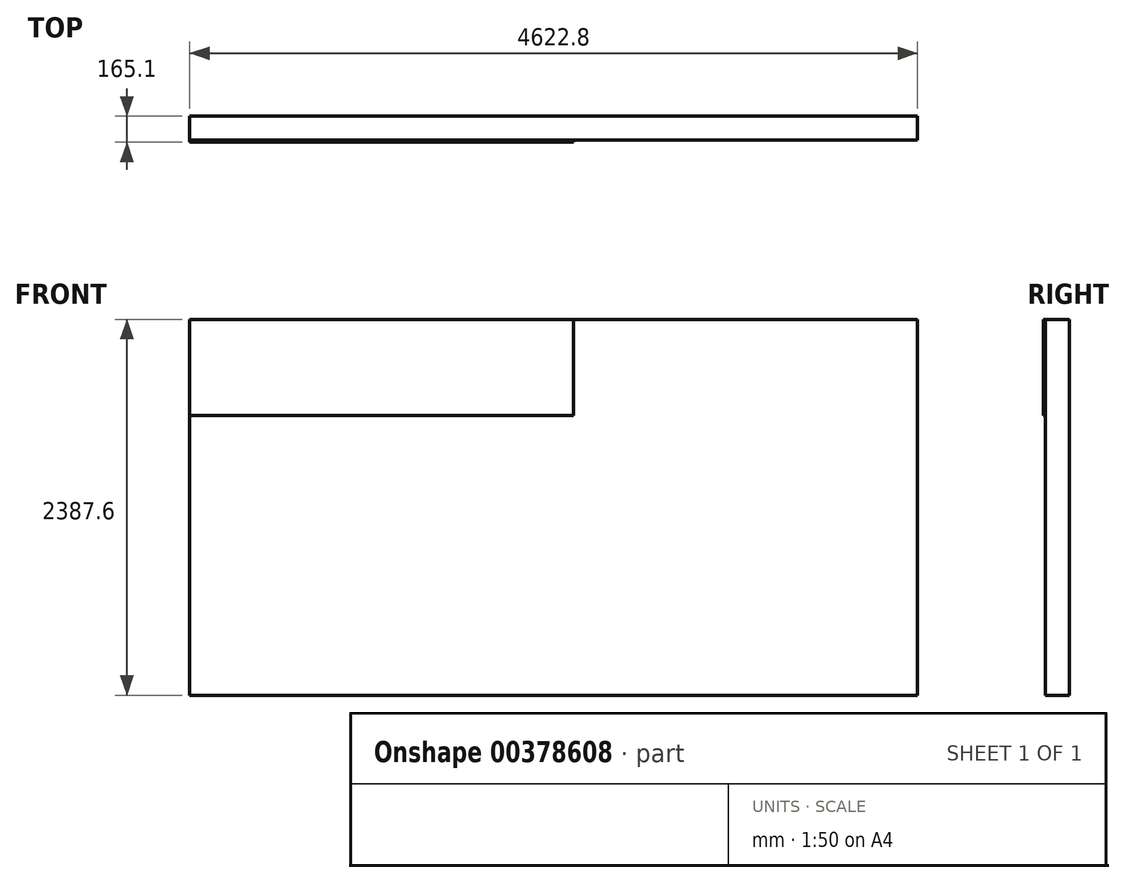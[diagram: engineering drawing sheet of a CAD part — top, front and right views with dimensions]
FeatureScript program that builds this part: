
annotation { "Feature Type Name" : "Feature", "Feature Type Description" : "" }
export const myFeature = defineFeature(function(context is Context, id is Id, definition is map)
    precondition{}
    {
        {
            var Q0;
            Q0=qCreatedBy(makeId("Front.planeOp"),FACE);
            var sketch = newSketch(context, id + "F0", { "sketchPlane" : qUnion([Q0])});
            skLineSegment(sketch, "E0.bottom", {"start": v(0, 0) * mm, "end": v(4622.8, 0) * mm});
            skLineSegment(sketch, "E0.top", {"start": v(0, 2387.6) * mm, "end": v(4622.8, 2387.6) * mm});
            skLineSegment(sketch, "E0.left", {"start": v(0, 0) * mm, "end": v(0, 2387.6) * mm});
            skLineSegment(sketch, "E0.right", {"start": v(4622.8, 0) * mm, "end": v(4622.8, 2387.6) * mm});
            skSolve(sketch);
        }
        {
            var Q0;
            Q0=makeQuery(id+"F0.imprint","IMPRINT",FACE,{"disambiguationData":[TD([[makeQuery(id+"F0.imprint","IMPRINT",EDGE,{"derivedFrom":sQuery(id+"F0.wireOp",EDGE,"E0.bottom")}),1.0]])]});
            extrude(context, id + "F1", {"entities" : qUnion([Q0]), "oppositeDirection" : true, "depth" : 152.4 * mm});
        }
        {
            var Q0;
            Q0=makeQuery(id+"F1.opExtrude","CAP_FACE",FACE,{"disambiguationData":[OSD([sQuery(id+"F0.wireOp",EDGE,"E0.bottom"),sQuery(id+"F0.wireOp",EDGE,"E0.top"),sQuery(id+"F0.wireOp",EDGE,"E0.left"),sQuery(id+"F0.wireOp",EDGE,"E0.right")])],"isStart":true});
            var sketch = newSketch(context, id + "F2", { "sketchPlane" : qUnion([Q0])});
            skLineSegment(sketch, "E1.bottom", {"start": v(0, 1778) * mm, "end": v(2438.4, 1778) * mm});
            skLineSegment(sketch, "E1.top", {"start": v(0, 2387.6) * mm, "end": v(2438.4, 2387.6) * mm});
            skLineSegment(sketch, "E1.left", {"start": v(0, 1778) * mm, "end": v(0, 2387.6) * mm});
            skLineSegment(sketch, "E1.right", {"start": v(2438.4, 1778) * mm, "end": v(2438.4, 2387.6) * mm});
            skSolve(sketch);
        }
        {
            var Q0;
            Q0 = qSketchRegion(id + "F2", true);
            extrude(context, id + "F3", {"entities" : qUnion([Q0]), "depth" : 12.7 * mm});
        }
    });
